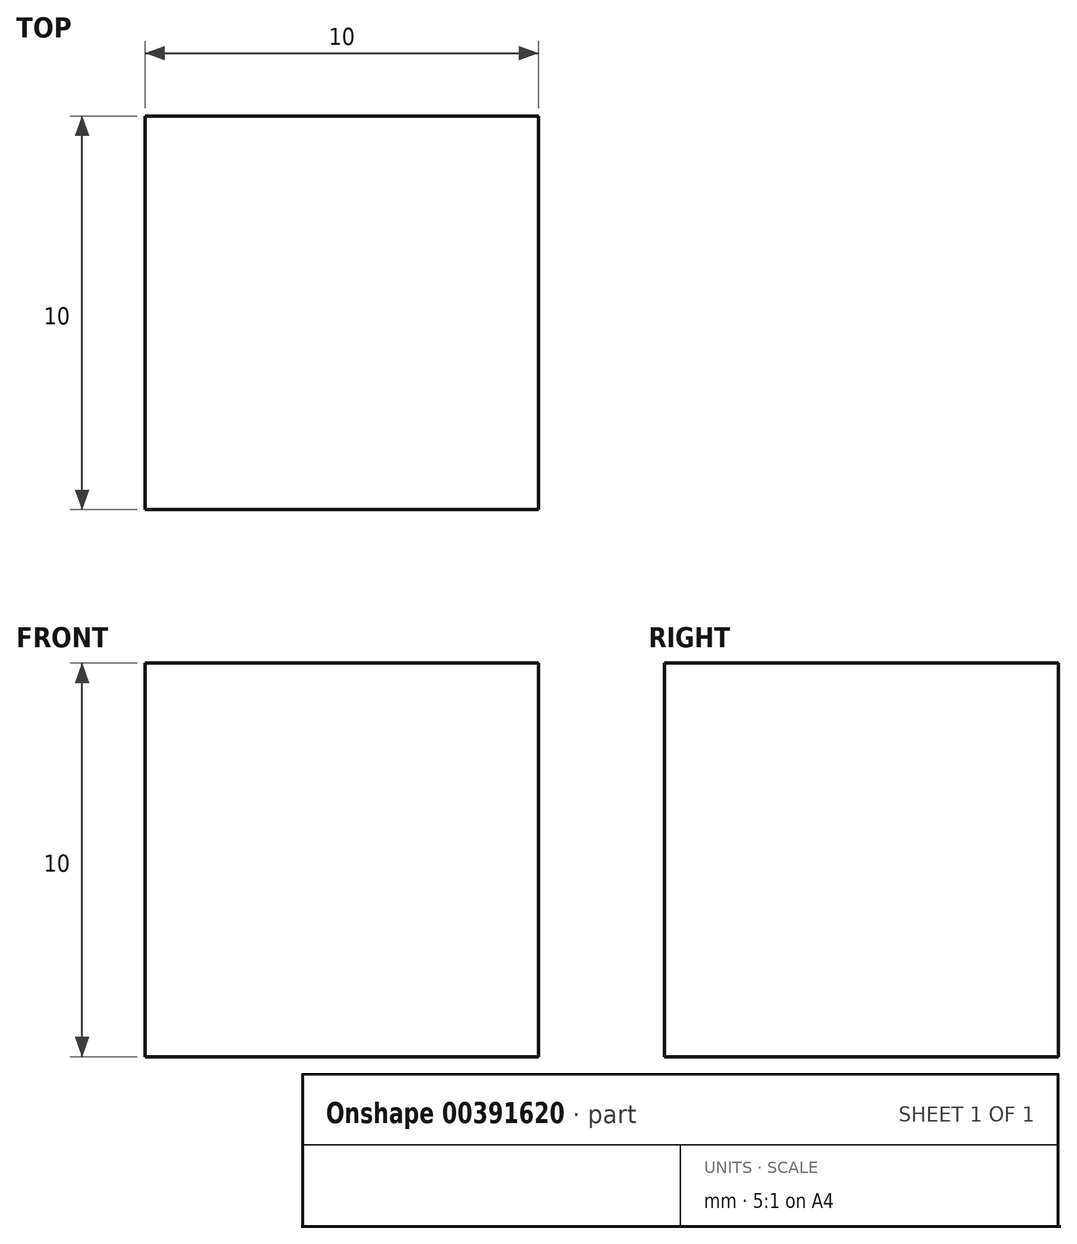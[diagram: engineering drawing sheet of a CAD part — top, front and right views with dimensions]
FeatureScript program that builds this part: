
annotation { "Feature Type Name" : "Feature", "Feature Type Description" : "" }
export const myFeature = defineFeature(function(context is Context, id is Id, definition is map)
    precondition{}
    {
        {
            var Q0;
            Q0=qCreatedBy(makeId("Front.planeOp"),FACE);
            var sketch = newSketch(context, id + "F0", { "sketchPlane" : qUnion([Q0])});
            skLineSegment(sketch, "E0.bottom", {"start": v(0, 10) * mm, "end": v(10, 10) * mm});
            skLineSegment(sketch, "E0.top", {"start": v(0, 0) * mm, "end": v(10, 0) * mm});
            skLineSegment(sketch, "E0.left", {"start": v(0, 10) * mm, "end": v(0, 0) * mm});
            skLineSegment(sketch, "E0.right", {"start": v(10, 10) * mm, "end": v(10, 0) * mm});
            skSolve(sketch);
        }
        {
            var Q0;
            Q0=makeQuery(id+"F0.imprint","IMPRINT",FACE,{"disambiguationData":[TD([[makeQuery(id+"F0.imprint","IMPRINT",EDGE,{"derivedFrom":sQuery(id+"F0.wireOp",EDGE,"E0.bottom")}),-1.0]])]});
            extrude(context, id + "F1", {"entities" : qUnion([Q0]), "depth" : 10 * mm});
        }
    });
